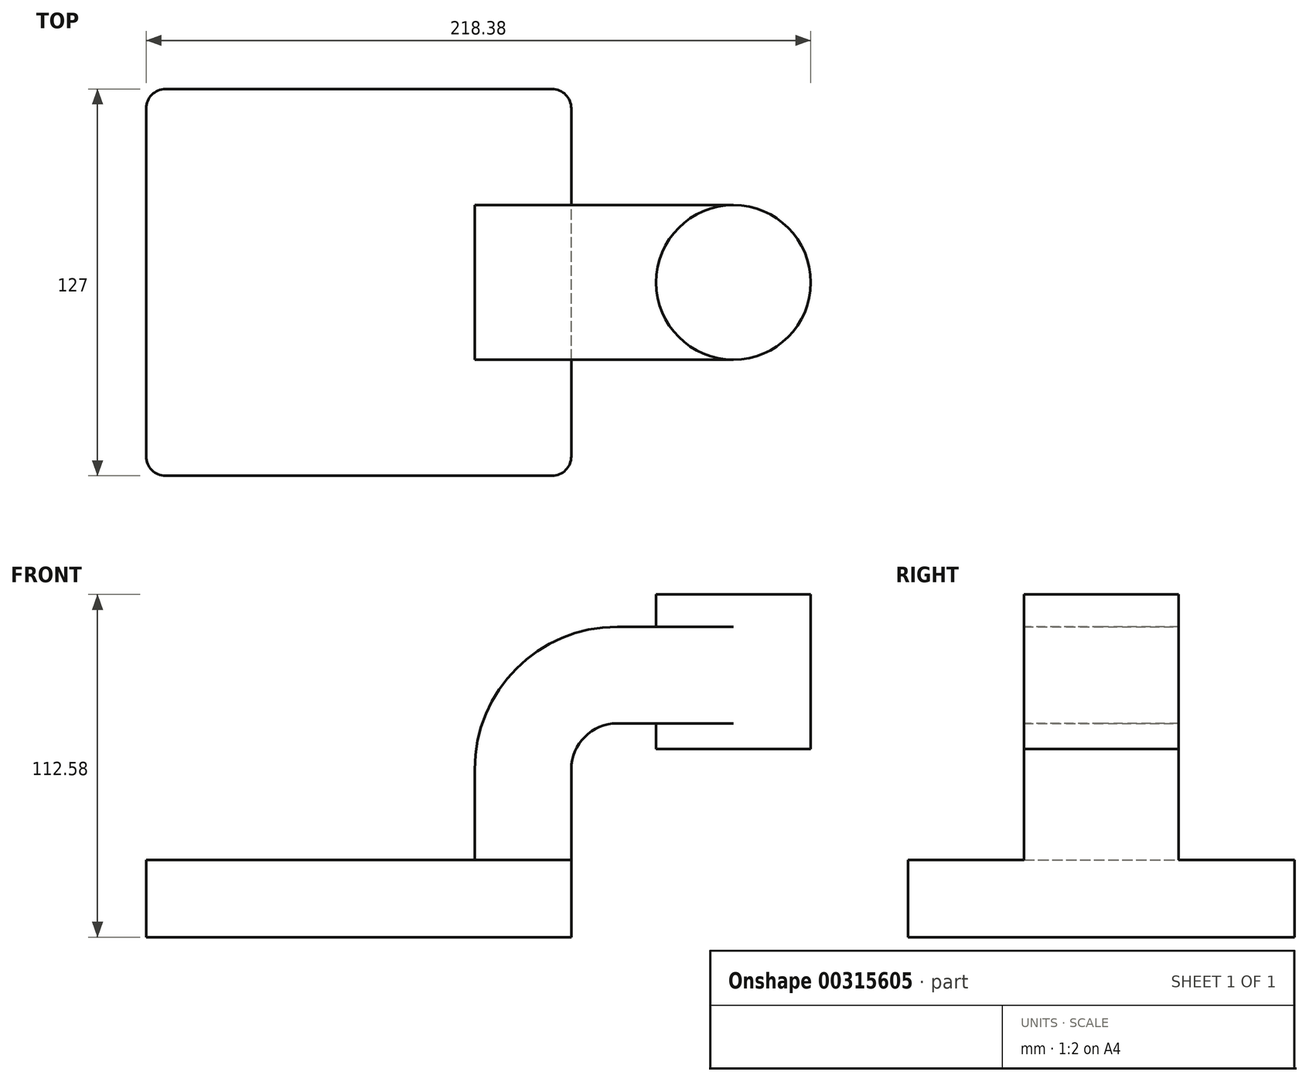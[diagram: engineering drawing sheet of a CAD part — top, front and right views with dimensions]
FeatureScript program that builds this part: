
annotation { "Feature Type Name" : "Feature", "Feature Type Description" : "" }
export const myFeature = defineFeature(function(context is Context, id is Id, definition is map)
    precondition{}
    {
        {
            var Q0;
            Q0=qCreatedBy(makeId("Front.planeOp"),FACE);
            var sketch = newSketch(context, id + "F0", { "sketchPlane" : qUnion([Q0])});
            skLineSegment(sketch, "E0.bottom", {"start": v(69.85, -12.7) * mm, "end": v(-69.85, -12.7) * mm});
            skLineSegment(sketch, "E0.top", {"start": v(69.85, 12.7) * mm, "end": v(-69.85, 12.7) * mm});
            skLineSegment(sketch, "E0.left", {"start": v(69.85, -12.7) * mm, "end": v(69.85, 12.7) * mm});
            skLineSegment(sketch, "E0.right", {"start": v(-69.85, -12.7) * mm, "end": v(-69.85, 12.7) * mm});
            skPoint(sketch, "E0.middle", {"position": v(0, 0) * mm});
            skLineSegment(sketch, "E1.bottom", {"start": v(148.53, 49.08) * mm, "end": v(97.73, 49.08) * mm});
            skLineSegment(sketch, "E1.top", {"start": v(148.53, 99.88) * mm, "end": v(97.73, 99.88) * mm});
            skLineSegment(sketch, "E1.left", {"start": v(148.53, 49.08) * mm, "end": v(148.53, 99.88) * mm});
            skLineSegment(sketch, "E1.right", {"start": v(97.73, 49.08) * mm, "end": v(97.73, 99.88) * mm});
            skPoint(sketch, "E1.middle", {"position": v(123.13, 74.48) * mm});
            skLineSegment(sketch, "E2", {"start": v(69.85, 12.7) * mm, "end": v(69.85, 42.42) * mm});
            skArc(sketch, "E3", {"start": v(69.85, 42.42) * mm, "mid": v(74.27, 53.1) * mm, "end": v(84.94, 57.51) * mm});
            skLineSegment(sketch, "E4", {"start": v(84.94, 57.51) * mm, "end": v(123.13, 57.51) * mm});
            skLineSegment(sketch, "E5", {"start": v(123.13, 49.08) * mm, "end": v(123.13, 99.88) * mm});
            skLineSegment(sketch, "E6.0", {"start": v(84.94, 89.26) * mm, "end": v(123.13, 89.26) * mm});
            skArc(sketch, "E6.1", {"start": v(38.1, 42.42) * mm, "mid": v(51.82, 75.54) * mm, "end": v(84.94, 89.26) * mm});
            skLineSegment(sketch, "E6.2", {"start": v(38.1, 12.7) * mm, "end": v(38.1, 42.42) * mm});
            skFitSpline(sketch, "E7", {"points": [v(-44.14, 12.7) * mm, v(97.73, 89.26) * mm], "startDerivative": vector(-4.01, 191.94) * mm, "endDerivative": vector(253.05, -9.07) * mm});
            skSolve(sketch);
        }
        {
            var Q0;
            Q0=makeQuery(id+"F0.imprint","IMPRINT",FACE,{"disambiguationData":[TD([[makeQuery(id+"F0.imprint","IMPRINT",EDGE,{"derivedFrom":sQuery(id+"F0.wireOp",EDGE,"E0.bottom")}),-1.0]])]});
            extrude(context, id + "F1", {"entities" : qUnion([Q0]), "endBound" : BoundingType.SYMMETRIC, "depth" : 127 * mm});
        }
        {
            var Q0;
            {var subQ1=sQuery(id+"F0.wireOp",EDGE,"E2");Q0=makeQuery(id+"F0.imprint","IMPRINT",FACE,{"disambiguationData":[TD([[makeQuery(id+"F0.imprint","IMPRINT",EDGE,{"derivedFrom":subQ1}),1.0]])]});}
            var Q1;
            {var subQ3=sQuery(id+"F0.wireOp",EDGE,"E4");var subQ5=sQuery(id+"F0.wireOp",EDGE,"E5");var subQ6=makeQuery(id+"F0.imprint","INTERSECT",VERTEX,{"derivedFrom":[subQ3,subQ5]});Q1=makeQuery(id+"F0.imprint","IMPRINT",FACE,{"disambiguationData":[TD([[makeQuery(id+"F0.imprint","IMPRINT",EDGE,{"disambiguationData":[TD([[subQ6,1.0]])],"derivedFrom":subQ3}),1.0]])]});}
            extrude(context, id + "F2", {"entities" : qUnion([Q0, Q1]), "operationType" : NewBodyOperationType.ADD, "endBound" : BoundingType.SYMMETRIC, "depth" : 50.8 * mm});
        }
        {
            var Q0;
            {var subQ3=sQuery(id+"F0.wireOp",EDGE,"E6.1");Q0=makeQuery(id+"F0.imprint","IMPRINT",FACE,{"disambiguationData":[TD([[makeQuery(id+"F0.imprint","IMPRINT",EDGE,{"derivedFrom":subQ3}),1.0]])]});}
            extrude(context, id + "F3", {"entities" : qUnion([Q0]), "operationType" : NewBodyOperationType.ADD, "endBound" : BoundingType.SYMMETRIC, "depth" : 38.1 * mm});
        }
        {
            var Q0;
            {var subQ0=sQuery(id+"F0.wireOp",EDGE,"E1.left");Q0=makeQuery(id+"F0.imprint","IMPRINT",FACE,{"disambiguationData":[TD([[makeQuery(id+"F0.imprint","IMPRINT",EDGE,{"derivedFrom":subQ0}),1.0]])]});}
            var Q1;
            Q1=sQuery(id+"F0.wireOp",EDGE,"E5");
            revolve(context, id + "F4", {"operationType" : NewBodyOperationType.ADD, "entities" : qUnion([Q0]), "axis" : qUnion([Q1]), "revolveType" : RevolveType.FULL});
        }
        {
            var Q0;
            Q0=makeQuery(id+"F1.opExtrude","CAP_EDGE",EDGE,{"disambiguationData":[OSD([sQuery(id+"F0.wireOp",EDGE,"E0.right")])],"isStart":true});
            var Q1;
            Q1=makeQuery(id+"F1.opExtrude","CAP_EDGE",EDGE,{"disambiguationData":[OSD([sQuery(id+"F0.wireOp",EDGE,"E0.left")])],"isStart":true});
            var Q2;
            Q2=makeQuery(id+"F1.opExtrude","CAP_EDGE",EDGE,{"disambiguationData":[OSD([sQuery(id+"F0.wireOp",EDGE,"E0.right")])],"isStart":false});
            var Q3;
            Q3=makeQuery(id+"F1.opExtrude","CAP_EDGE",EDGE,{"disambiguationData":[OSD([sQuery(id+"F0.wireOp",EDGE,"E0.left")])],"isStart":false});
            fillet(context, id + "F5", {"entities" : qUnion([Q0, Q1, Q2, Q3]), "radius" : 6.35 * mm, "tangentPropagation" : true, "allowEdgeOverflow" : false});
        }
    });
